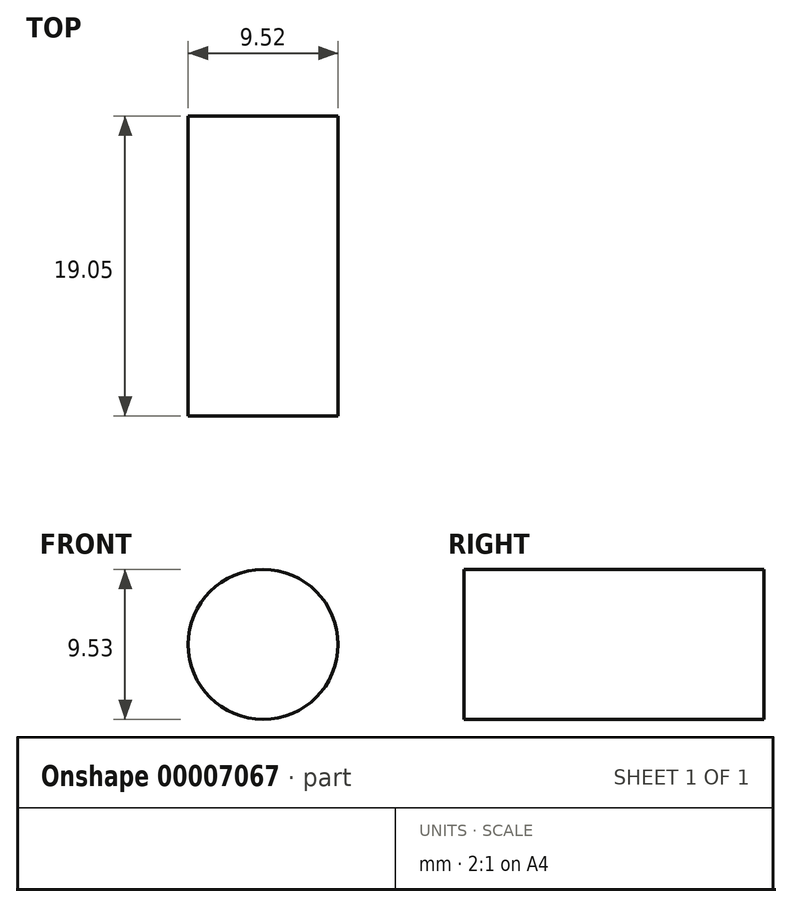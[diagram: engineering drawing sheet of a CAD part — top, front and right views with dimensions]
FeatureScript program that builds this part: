
annotation { "Feature Type Name" : "Feature", "Feature Type Description" : "" }
export const myFeature = defineFeature(function(context is Context, id is Id, definition is map)
    precondition{}
    {
        {
            var Q0;
            Q0=qCreatedBy(makeId("Right.planeOp"),FACE);
            var sketch = newSketch(context, id + "F0", { "sketchPlane" : qUnion([Q0])});
            skLineSegment(sketch, "E0", {"start": v(0, 0) * mm, "end": v(101.6, 0) * mm});
            skLineSegment(sketch, "E1", {"start": v(0, 0) * mm, "end": v(0, 165.1) * mm});
            skLineSegment(sketch, "E2.0", {"start": v(38.1, 19.05) * mm, "end": v(85.73, 19.05) * mm});
            skLineSegment(sketch, "E3.0", {"start": v(19.05, 38.1) * mm, "end": v(19.05, 165.1) * mm});
            skPoint(sketch, "E4.visualSharp", {"position": v(19.05, 19.05) * mm});
            skArc(sketch, "E4.filletArc", {"start": v(19.05, 38.1) * mm, "mid": v(24.63, 24.63) * mm, "end": v(38.1, 19.05) * mm});
            skLineSegment(sketch, "E5", {"start": v(101.6, 0) * mm, "end": v(101.6, 3.18) * mm});
            skArc(sketch, "E6.filletArc", {"start": v(101.6, 3.18) * mm, "mid": v(96.95, 14.4) * mm, "end": v(85.73, 19.05) * mm});
            skLineSegment(sketch, "E7", {"start": v(0, 165.1) * mm, "end": v(19.05, 165.1) * mm});
            skSolve(sketch);
        }
        {
            var Q0;
            Q0=qSketchRegion(id+"F0",true);
            extrude(context, id + "F1", {"entities" : qUnion([Q0]), "endBound" : BoundingType.SYMMETRIC, "depth" : 152.4 * mm});
        }
        {
            var Q0;
            Q0=makeQuery(id+"F1.opExtrude","CAP_EDGE",EDGE,{"disambiguationData":[OSD([sQuery(id+"F0.wireOp",EDGE,"E7")])],"isStart":false});
            var Q1;
            Q1=makeQuery(id+"F1.opExtrude","CAP_EDGE",EDGE,{"disambiguationData":[OSD([sQuery(id+"F0.wireOp",EDGE,"E7")])],"isStart":true});
            chamfer(context, id + "F2", {"entities" : qUnion([Q0, Q1]), "width" : 19.05 * mm, "tangentPropagation" : true});
        }
        {
            var Q0;
            Q0=makeQuery(id+"F1.opExtrude","SWEPT_FACE",FACE,{"disambiguationData":[OSD([sQuery(id+"F0.wireOp",EDGE,"E1")])]});
            var sketch = newSketch(context, id + "F3", { "sketchPlane" : qUnion([Q0])});
            skLineSegment(sketch, "E8", {"start": v(0, 165.1) * mm, "end": v(0, 0) * mm, "construction": true});
            skLineSegment(sketch, "E9.0", {"start": v(82.55, 114.3) * mm, "end": v(-82.55, 114.3) * mm, "construction": true});
            skArc(sketch, "E10", {"start": v(-28.58, 114.3) * mm, "mid": v(0, 85.73) * mm, "end": v(28.58, 114.3) * mm});
            skLineSegment(sketch, "E11", {"start": v(-28.58, 114.3) * mm, "end": v(-28.58, 200.77) * mm});
            skLineSegment(sketch, "E12", {"start": v(28.58, 114.3) * mm, "end": v(28.58, 203.32) * mm});
            skLineSegment(sketch, "E13", {"start": v(28.58, 203.32) * mm, "end": v(-28.58, 200.77) * mm});
            skSolve(sketch);
        }
        {
            var Q0;
            {var subQ3=sQuery(id+"F3.wireOp",EDGE,"E10");Q0=makeQuery(id+"F3.imprint","IMPRINT",FACE,{"disambiguationData":[TD([[makeQuery(id+"F3.imprint","IMPRINT",EDGE,{"derivedFrom":subQ3}),1.0]])]});}
            extrude(context, id + "F4", {"entities" : qUnion([Q0]), "operationType" : NewBodyOperationType.REMOVE, "endBound" : BoundingType.THROUGH_ALL, "oppositeDirection" : true, "depth" : 25.4 * mm});
        }
        {
            var Q0;
            Q0=makeQuery(id+"F1.opExtrude","SWEPT_FACE",FACE,{"disambiguationData":[OSD([sQuery(id+"F0.wireOp",EDGE,"E0")])]});
            var sketch = newSketch(context, id + "F5", { "sketchPlane" : qUnion([Q0])});
            skLineSegment(sketch, "E14.0", {"start": v(76.2, 0) * mm, "end": v(-76.2, 0) * mm, "construction": true});
            skLineSegment(sketch, "E15", {"start": v(0, 34.37) * mm, "end": v(0, -116.49) * mm, "construction": true});
            skLineSegment(sketch, "E16.0", {"start": v(82.55, -66.55) * mm, "end": v(-82.55, -66.55) * mm, "construction": true});
            skLineSegment(sketch, "E17.0", {"start": v(57.15, 34.37) * mm, "end": v(57.15, -116.49) * mm, "construction": true});
            skCircle(sketch, "E18", {"center": v(57.15, -66.55) * mm, "radius": 8.73 * mm});
            skCircle(sketch, "E19.0.MirrorC", {"center": v(-57.15, -66.55) * mm, "radius": 8.73 * mm});
            skSolve(sketch);
        }
        {
            var Q0;
            Q0=qSketchRegion(id+"F5",true);
            extrude(context, id + "F6", {"entities" : qUnion([Q0]), "operationType" : NewBodyOperationType.REMOVE, "endBound" : BoundingType.THROUGH_ALL, "oppositeDirection" : true, "depth" : 25.4 * mm});
        }
        {
            var Q0;
            Q0=makeQuery(id+"F1.opExtrude","SWEPT_FACE",FACE,{"disambiguationData":[OSD([sQuery(id+"F0.wireOp",EDGE,"E1")])]});
            var sketch = newSketch(context, id + "F7", { "sketchPlane" : qUnion([Q0])});
            skLineSegment(sketch, "E20", {"start": v(0, -27.81) * mm, "end": v(0, 198.51) * mm, "construction": true});
            skLineSegment(sketch, "E21", {"start": v(-110.83, 114.3) * mm, "end": v(104.76, 114.3) * mm, "construction": true});
            skLineSegment(sketch, "E22.0", {"start": v(-110.83, 149.22) * mm, "end": v(104.76, 149.23) * mm, "construction": true});
            skLineSegment(sketch, "E23.0", {"start": v(-38.1, -27.81) * mm, "end": v(-38.1, 198.51) * mm, "construction": true});
            skCircle(sketch, "E24", {"center": v(-38.1, 149.23) * mm, "radius": 4.76 * mm});
            skCircle(sketch, "E25.0.MirrorC", {"center": v(38.1, 149.23) * mm, "radius": 4.76 * mm});
            skSolve(sketch);
        }
        {
            var Q0;
            Q0=makeQuery(id+"F7.imprint","IMPRINT",FACE,{"disambiguationData":[TD([[makeQuery(id+"F7.imprint","IMPRINT",EDGE,{"derivedFrom":sQuery(id+"F7.wireOp",EDGE,"E24")}),1.0]])]});
            var Q1;
            Q1=makeQuery(id+"F7.imprint","IMPRINT",FACE,{"disambiguationData":[TD([[makeQuery(id+"F7.imprint","IMPRINT",EDGE,{"derivedFrom":sQuery(id+"F7.wireOp",EDGE,"E25.0.MirrorC")}),-1.0]])]});
            extrude(context, id + "F8", {"entities" : qUnion([Q0, Q1]), "operationType" : NewBodyOperationType.REMOVE, "endBound" : BoundingType.THROUGH_ALL, "oppositeDirection" : true, "depth" : 25.4 * mm});
        }
    });
